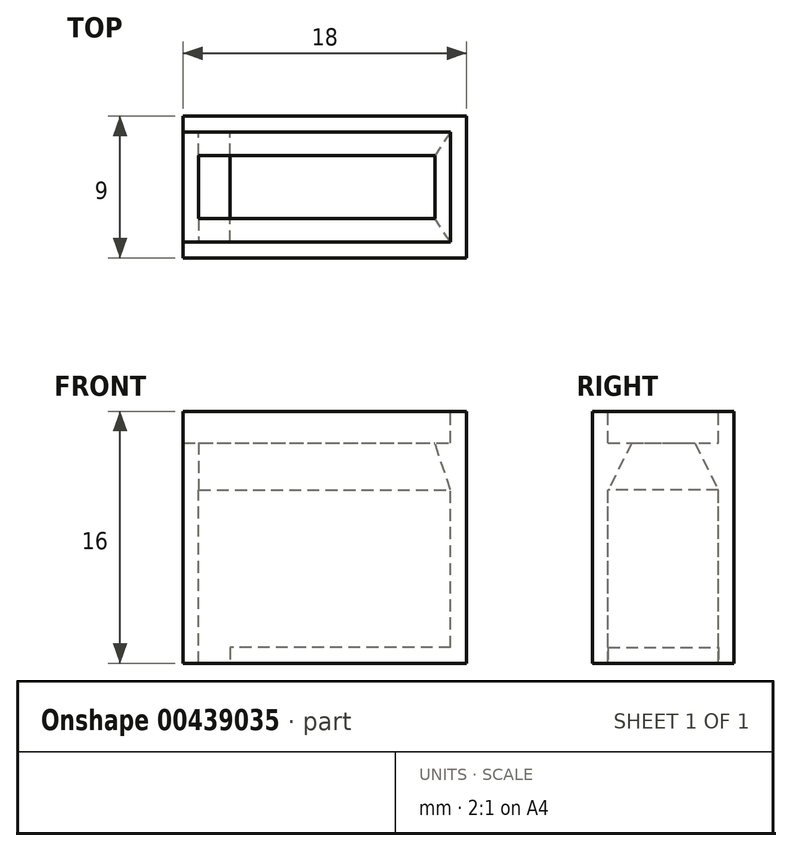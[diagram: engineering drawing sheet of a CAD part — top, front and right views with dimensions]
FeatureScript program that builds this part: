
annotation { "Feature Type Name" : "Feature", "Feature Type Description" : "" }
export const myFeature = defineFeature(function(context is Context, id is Id, definition is map)
    precondition{}
    {
        {
            var Q0;
            Q0=qCreatedBy(makeId("Top.planeOp"),FACE);
            var sketch = newSketch(context, id + "F0", { "sketchPlane" : qUnion([Q0])});
            skLineSegment(sketch, "E0.bottom", {"start": v(9, -4.5) * mm, "end": v(-9, -4.5) * mm});
            skLineSegment(sketch, "E0.top", {"start": v(9, 4.5) * mm, "end": v(-9, 4.5) * mm});
            skLineSegment(sketch, "E0.left", {"start": v(9, -4.5) * mm, "end": v(9, 4.5) * mm});
            skLineSegment(sketch, "E0.right", {"start": v(-9, -4.5) * mm, "end": v(-9, 4.5) * mm});
            skPoint(sketch, "E0.middle", {"position": v(0, 0) * mm});
            skSolve(sketch);
        }
        {
            var Q0;
            Q0=qSketchRegion(id+"F0",true);
            extrude(context, id + "F1", {"entities" : qUnion([Q0]), "depth" : 14 * mm});
        }
        {
            var Q0;
            Q0=makeQuery(id+"F1.opExtrude","CAP_FACE",FACE,{"disambiguationData":[OSD([sQuery(id+"F0.wireOp",EDGE,"E0.bottom"),sQuery(id+"F0.wireOp",EDGE,"E0.top"),sQuery(id+"F0.wireOp",EDGE,"E0.left"),sQuery(id+"F0.wireOp",EDGE,"E0.right")])],"isStart":false});
            var sketch = newSketch(context, id + "F2", { "sketchPlane" : qUnion([Q0])});
            skLineSegment(sketch, "E1.bottom", {"start": v(8, -3.5) * mm, "end": v(-8, -3.5) * mm});
            skLineSegment(sketch, "E1.top", {"start": v(8, 3.5) * mm, "end": v(-8, 3.5) * mm});
            skLineSegment(sketch, "E1.left", {"start": v(8, -3.5) * mm, "end": v(8, 3.5) * mm});
            skLineSegment(sketch, "E1.right", {"start": v(-8, -3.5) * mm, "end": v(-8, 3.5) * mm});
            skPoint(sketch, "E1.middle", {"position": v(0, 0) * mm});
            skSolve(sketch);
        }
        {
            var Q0;
            Q0=qSketchRegion(id+"F2",true);
            extrude(context, id + "F3", {"entities" : qUnion([Q0]), "operationType" : NewBodyOperationType.REMOVE, "oppositeDirection" : true, "depth" : 13 * mm});
        }
        {
            var Q0;
            Q0=makeQuery(id+"F1.opExtrude","CAP_FACE",FACE,{"disambiguationData":[OSD([sQuery(id+"F0.wireOp",EDGE,"E0.bottom"),sQuery(id+"F0.wireOp",EDGE,"E0.top"),sQuery(id+"F0.wireOp",EDGE,"E0.left"),sQuery(id+"F0.wireOp",EDGE,"E0.right")])],"isStart":true});
            var sketch = newSketch(context, id + "F4", { "sketchPlane" : qUnion([Q0])});
            skLineSegment(sketch, "E2.bottom", {"start": v(4.1, -2) * mm, "end": v(0.1, -2) * mm, "construction": true});
            skLineSegment(sketch, "E2.top", {"start": v(4.1, 2) * mm, "end": v(0.1, 2) * mm, "construction": true});
            skLineSegment(sketch, "E2.left", {"start": v(4.1, -2) * mm, "end": v(4.1, 2) * mm, "construction": true});
            skLineSegment(sketch, "E2.right", {"start": v(0.1, -2) * mm, "end": v(0.1, 2) * mm, "construction": true});
            skPoint(sketch, "E2.middle", {"position": v(2.1, 0) * mm});
            skLineSegment(sketch, "E3.bottom", {"start": v(-6, -3.5) * mm, "end": v(-8, -3.5) * mm});
            skLineSegment(sketch, "E3.top", {"start": v(-6, 3.5) * mm, "end": v(-8, 3.5) * mm});
            skLineSegment(sketch, "E3.left", {"start": v(-6, -3.5) * mm, "end": v(-6, 3.5) * mm});
            skLineSegment(sketch, "E3.right", {"start": v(-8, -3.5) * mm, "end": v(-8, 3.5) * mm});
            skPoint(sketch, "E3.middle", {"position": v(-7, 0) * mm});
            skSolve(sketch);
        }
        {
            var Q0;
            Q0=qSketchRegion(id+"F4",true);
            extrude(context, id + "F5", {"entities" : qUnion([Q0]), "operationType" : NewBodyOperationType.REMOVE, "oppositeDirection" : true, "depth" : 6 * mm});
        }
        {
            var Q0;
            Q0=makeQuery(id+"F4.imprint","IMPRINT",FACE,{"disambiguationData":[TD([[makeQuery(id+"F4.imprint","IMPRINT",EDGE,{"derivedFrom":sQuery(id+"F4.wireOp",EDGE,"E3.bottom")}),-1.0]])]});
            extrude(context, id + "F6", {"entities" : qUnion([Q0]), "operationType" : NewBodyOperationType.REMOVE, "oppositeDirection" : true, "depth" : 9 * mm});
        }
        {
            var Q0;
            Q0=makeQuery(id+"F1.opExtrude","CAP_FACE",FACE,{"disambiguationData":[OSD([sQuery(id+"F0.wireOp",EDGE,"E0.bottom"),sQuery(id+"F0.wireOp",EDGE,"E0.top"),sQuery(id+"F0.wireOp",EDGE,"E0.left"),sQuery(id+"F0.wireOp",EDGE,"E0.right")])],"isStart":false});
            var sketch = newSketch(context, id + "F7", { "sketchPlane" : qUnion([Q0])});
            skLineSegment(sketch, "E4", {"start": v(-9, 4.5) * mm, "end": v(9, 4.5) * mm});
            skLineSegment(sketch, "E5", {"start": v(9, 4.5) * mm, "end": v(9, -4.5) * mm});
            skLineSegment(sketch, "E6", {"start": v(9, -4.5) * mm, "end": v(-9, -4.5) * mm});
            skLineSegment(sketch, "E7", {"start": v(-9, -4.5) * mm, "end": v(-9, -3.5) * mm});
            skLineSegment(sketch, "E8", {"start": v(-9, -3.5) * mm, "end": v(8, -3.5) * mm});
            skLineSegment(sketch, "E9", {"start": v(8, -3.5) * mm, "end": v(8, 3.5) * mm});
            skLineSegment(sketch, "E10", {"start": v(8, 3.5) * mm, "end": v(-9, 3.5) * mm});
            skLineSegment(sketch, "E11", {"start": v(-9, 3.5) * mm, "end": v(-9, 4.5) * mm});
            skSolve(sketch);
        }
        {
            var Q0;
            Q0=qSketchRegion(id+"F7",true);
            extrude(context, id + "F8", {"entities" : qUnion([Q0]), "operationType" : NewBodyOperationType.ADD, "depth" : 2 * mm});
        }
        {
            var Q0;
            Q0=makeQuery(id+"F8.boolean.opBoolean","MERGE",FACE,{"derivedFrom":[makeQuery(id+"F6.boolean.opBoolean","MERGE",FACE,{"derivedFrom":[makeQuery(id+"F3.boolean.opBoolean","COPY",FACE,{"derivedFrom":makeQuery(id+"F3.opExtrude","SWEPT_FACE",FACE,{"disambiguationData":[OSD([sQuery(id+"F2.wireOp",EDGE,"E1.bottom")])]})}),makeQuery(id+"F6.opExtrude","SWEPT_FACE",FACE,{"disambiguationData":[OSD([sQuery(id+"F4.wireOp",EDGE,"E3.top")])]})]}),makeQuery(id+"F8.opExtrude","SWEPT_FACE",FACE,{"disambiguationData":[OSD([sQuery(id+"F7.wireOp",EDGE,"E8")])]})]});
            var sketch = newSketch(context, id + "F9", { "sketchPlane" : qUnion([Q0])});
            skLineSegment(sketch, "E12", {"start": v(-8, 14) * mm, "end": v(-7, 14) * mm});
            skLineSegment(sketch, "E13", {"start": v(8, 14) * mm, "end": v(6.5, 14) * mm, "construction": true});
            skLineSegment(sketch, "E14", {"start": v(6.5, 14) * mm, "end": v(8, 7) * mm, "construction": true});
            skLineSegment(sketch, "E15", {"start": v(8, 7) * mm, "end": v(8, 14) * mm, "construction": true});
            skLineSegment(sketch, "E16", {"start": v(-7, 14) * mm, "end": v(-8, 11) * mm});
            skLineSegment(sketch, "E17", {"start": v(-8, 11) * mm, "end": v(-8, 14) * mm});
            skSolve(sketch);
        }
        {
            var Q0;
            Q0=qSketchRegion(id+"F9",true);
            extrude(context, id + "F10", {"entities" : qUnion([Q0]), "depth" : 7 * mm});
        }
        {
            var Q0;
            Q0=makeQuery(id+"F8.boolean.opBoolean","MERGE",FACE,{"derivedFrom":[makeQuery(id+"F3.boolean.opBoolean","COPY",FACE,{"derivedFrom":makeQuery(id+"F3.opExtrude","SWEPT_FACE",FACE,{"disambiguationData":[OSD([sQuery(id+"F2.wireOp",EDGE,"E1.left")])]})}),makeQuery(id+"F8.opExtrude","SWEPT_FACE",FACE,{"disambiguationData":[OSD([sQuery(id+"F7.wireOp",EDGE,"E9")])]})]});
            var sketch = newSketch(context, id + "F11", { "sketchPlane" : qUnion([Q0])});
            skLineSegment(sketch, "E18", {"start": v(3.5, 14) * mm, "end": v(2, 14) * mm});
            skLineSegment(sketch, "E19", {"start": v(-2, 14) * mm, "end": v(-3.5, 14) * mm});
            skLineSegment(sketch, "E20", {"start": v(2, 14) * mm, "end": v(3.5, 11) * mm});
            skLineSegment(sketch, "E21", {"start": v(3.5, 11) * mm, "end": v(3.5, 14) * mm});
            skLineSegment(sketch, "E22", {"start": v(-2, 14) * mm, "end": v(-3.5, 11) * mm});
            skLineSegment(sketch, "E23", {"start": v(-3.5, 11) * mm, "end": v(-3.5, 14) * mm});
            skSolve(sketch);
        }
        {
            var Q0;
            Q0=qSketchRegion(id+"F11",true);
            extrude(context, id + "F12", {"entities" : qUnion([Q0]), "operationType" : NewBodyOperationType.ADD, "depth" : 16 * mm});
        }
    });
